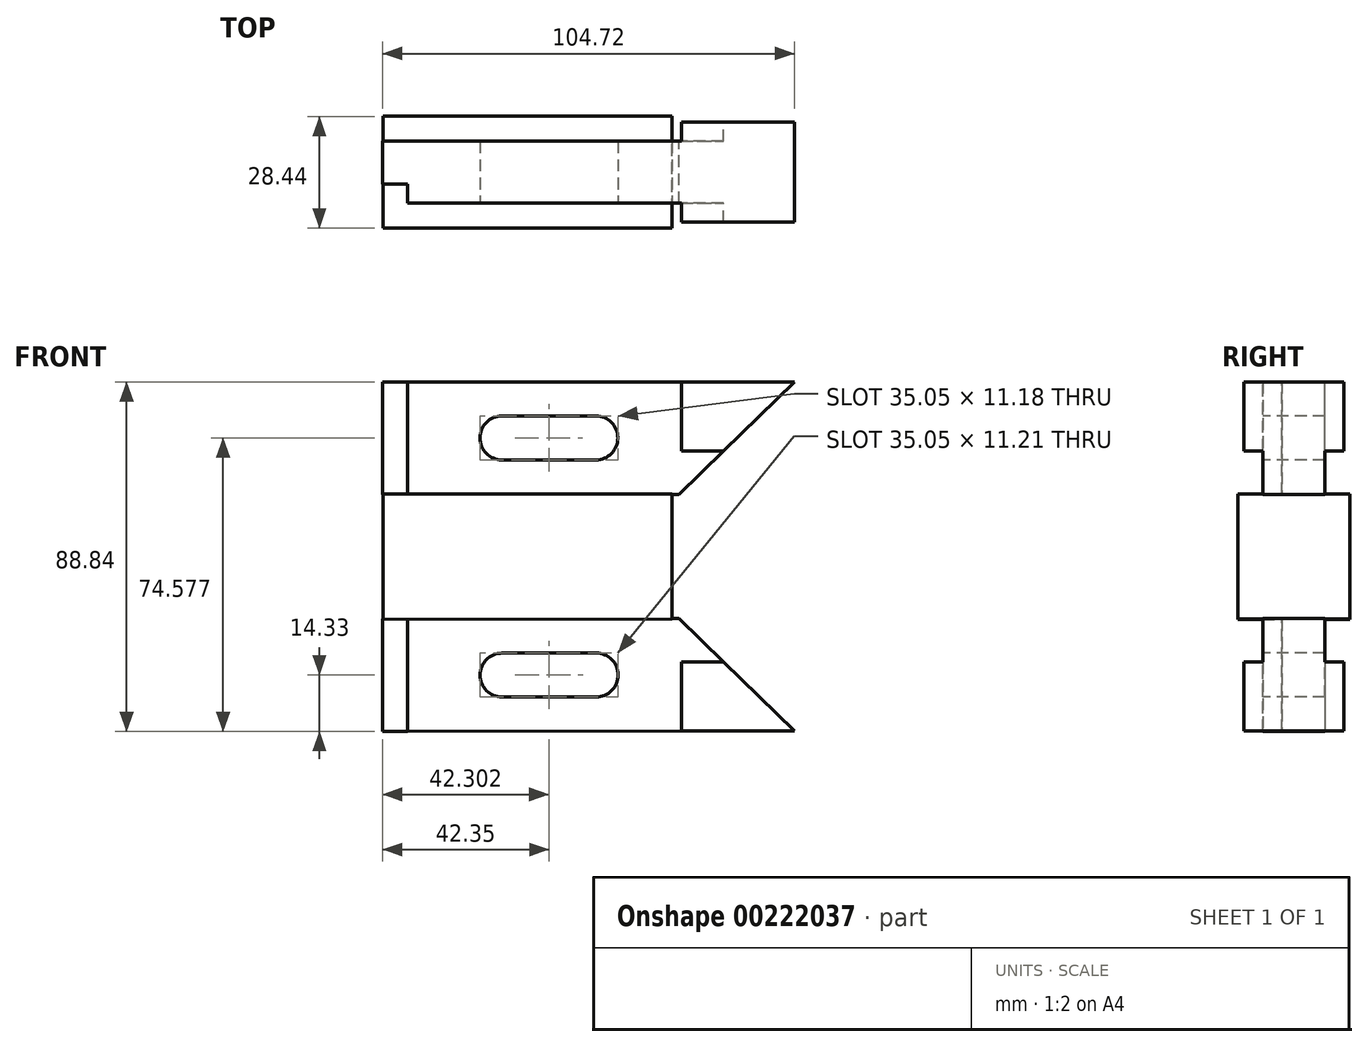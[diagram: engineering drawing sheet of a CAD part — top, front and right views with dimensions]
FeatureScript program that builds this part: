
annotation { "Feature Type Name" : "Feature", "Feature Type Description" : "" }
export const myFeature = defineFeature(function(context is Context, id is Id, definition is map)
    precondition{}
    {
        {
            var Q0;
            Q0=qCreatedBy(makeId("Front.planeOp"),FACE);
            var sketch = newSketch(context, id + "F0", { "sketchPlane" : qUnion([Q0])});
            skLineSegment(sketch, "E0", {"start": v(42.72, -44.4) * mm, "end": v(36.25, -44.4) * mm});
            skLineSegment(sketch, "E1", {"start": v(36.25, -44.4) * mm, "end": v(36.25, -15.82) * mm, "construction": true});
            skLineSegment(sketch, "E2", {"start": v(32.3, 15.93) * mm, "end": v(32.3, 0.06) * mm});
            skLineSegment(sketch, "E3", {"start": v(-41.1, 15.93) * mm, "end": v(-41.1, 0) * mm});
            skLineSegment(sketch, "E4", {"start": v(-41.1, 15.93) * mm, "end": v(32.3, 15.93) * mm});
            skLineSegment(sketch, "E5", {"start": v(32.3, 0.06) * mm, "end": v(-41.1, 0) * mm});
            skPoint(sketch, "E6.orphan", {"position": v(32.3, -15.82) * mm});
            skSolve(sketch);
        }
        {
            var Q0;
            Q0=makeQuery(id+"F0.imprint","IMPRINT",FACE,{"disambiguationData":[TD([[makeQuery(id+"F0.imprint","IMPRINT",EDGE,{"derivedFrom":sQuery(id+"F0.wireOp",EDGE,"E2")}),-1.0]])]});
            extrude(context, id + "F1", {"entities" : qUnion([Q0]), "endBound" : BoundingType.SYMMETRIC, "depth" : 28.45 * mm});
        }
        {
            var Q0;
            Q0=qCreatedBy(makeId("Front.planeOp"),FACE);
            var sketch = newSketch(context, id + "F2", { "sketchPlane" : qUnion([Q0])});
            skLineSegment(sketch, "E7.0", {"start": v(-41.1, 15.93) * mm, "end": v(32.3, 15.93) * mm});
            skLineSegment(sketch, "E8.bottom", {"start": v(-41.24, 15.85) * mm, "end": v(63.4, 15.85) * mm});
            skLineSegment(sketch, "E8.top", {"start": v(-41.24, 44.42) * mm, "end": v(63.4, 44.42) * mm});
            skLineSegment(sketch, "E8.left", {"start": v(-41.24, 15.85) * mm, "end": v(-41.24, 44.42) * mm});
            skLineSegment(sketch, "E8.right", {"start": v(63.4, 15.85) * mm, "end": v(63.4, 44.42) * mm});
            skSolve(sketch);
        }
        {
            var Q0;
            Q0=makeQuery(id+"F2.imprint","IMPRINT",FACE,{"disambiguationData":[TD([[makeQuery(id+"F2.imprint","IMPRINT",EDGE,{"derivedFrom":sQuery(id+"F2.wireOp",EDGE,"E8.bottom")}),1.0]])]});
            extrude(context, id + "F3", {"entities" : qUnion([Q0]), "operationType" : NewBodyOperationType.ADD, "endBound" : BoundingType.SYMMETRIC, "depth" : 15.75 * mm});
        }
        {
            var Q0;
            Q0=makeQuery(id+"F3.opExtrude","CAP_FACE",FACE,{"disambiguationData":[OSD([sQuery(id+"F2.wireOp",EDGE,"E8.bottom"),sQuery(id+"F2.wireOp",EDGE,"E8.top"),sQuery(id+"F2.wireOp",EDGE,"E8.left"),sQuery(id+"F2.wireOp",EDGE,"E8.right")])],"isStart":false});
            var sketch = newSketch(context, id + "F4", { "sketchPlane" : qUnion([Q0])});
            skLineSegment(sketch, "E9.bottom", {"start": v(-41.24, 44.42) * mm, "end": v(-34.9, 44.42) * mm});
            skLineSegment(sketch, "E9.top", {"start": v(-41.24, 15.85) * mm, "end": v(-34.9, 15.85) * mm});
            skLineSegment(sketch, "E9.left", {"start": v(-41.24, 44.42) * mm, "end": v(-41.24, 15.85) * mm});
            skLineSegment(sketch, "E9.right", {"start": v(-34.9, 44.42) * mm, "end": v(-34.9, 15.85) * mm});
            skSolve(sketch);
        }
        {
            var Q0;
            {var subQ2=sQuery(id+"F4.wireOp",EDGE,"E9.bottom");Q0=makeQuery(id+"F4.imprint","IMPRINT",FACE,{"disambiguationData":[TD([[makeQuery(id+"F4.imprint","IMPRINT",EDGE,{"derivedFrom":subQ2}),-1.0]])]});}
            extrude(context, id + "F5", {"entities" : qUnion([Q0]), "operationType" : NewBodyOperationType.REMOVE, "oppositeDirection" : true, "depth" : 4.83 * mm});
        }
        {
            var Q0;
            Q0=qCreatedBy(makeId("Front.planeOp"),FACE);
            var sketch = newSketch(context, id + "F6", { "sketchPlane" : qUnion([Q0])});
            skLineSegment(sketch, "E10.0", {"start": v(-34.9, 44.42) * mm, "end": v(63.4, 44.42) * mm});
            skLineSegment(sketch, "E11.bottom", {"start": v(34.7, 44.42) * mm, "end": v(63.4, 44.42) * mm});
            skLineSegment(sketch, "E11.top", {"start": v(34.7, 26.9) * mm, "end": v(63.4, 26.9) * mm});
            skLineSegment(sketch, "E11.left", {"start": v(34.7, 44.42) * mm, "end": v(34.7, 26.9) * mm});
            skLineSegment(sketch, "E11.right", {"start": v(63.4, 44.42) * mm, "end": v(63.4, 26.9) * mm});
            skSolve(sketch);
        }
        {
            var Q0;
            Q0 = qSketchRegion(id + "F6", true);
            extrude(context, id + "F7", {"entities" : qUnion([Q0]), "operationType" : NewBodyOperationType.ADD, "endBound" : BoundingType.SYMMETRIC, "depth" : 25.4 * mm});
        }
        {
            var Q0;
            Q0=qCreatedBy(makeId("Front.planeOp"),FACE);
            var sketch = newSketch(context, id + "F8", { "sketchPlane" : qUnion([Q0])});
            skPoint(sketch, "E12.0", {"position": v(63.4, 44.42) * mm});
            skPoint(sketch, "E13.0", {"position": v(63.4, 15.85) * mm});
            skPoint(sketch, "E14.0", {"position": v(32.3, 15.85) * mm});
            skLineSegment(sketch, "E15", {"start": v(34.05, 15.82) * mm, "end": v(63.4, 44.42) * mm});
            skLineSegment(sketch, "E16", {"start": v(34.05, 15.82) * mm, "end": v(63.4, 15.85) * mm});
            skLineSegment(sketch, "E17", {"start": v(63.4, 44.42) * mm, "end": v(63.4, 15.85) * mm});
            skSolve(sketch);
        }
        {
            var Q0;
            Q0 = qSketchRegion(id + "F8", true);
            extrude(context, id + "F9", {"entities" : qUnion([Q0]), "operationType" : NewBodyOperationType.REMOVE, "endBound" : BoundingType.SYMMETRIC, "oppositeDirection" : true, "depth" : 25.4 * mm});
        }
        {
            var Q0;
            Q0=makeQuery(id+"F3.opExtrude","CAP_FACE",FACE,{"disambiguationData":[OSD([sQuery(id+"F2.wireOp",EDGE,"E8.bottom"),sQuery(id+"F2.wireOp",EDGE,"E8.top"),sQuery(id+"F2.wireOp",EDGE,"E8.left"),sQuery(id+"F2.wireOp",EDGE,"E8.right")])],"isStart":false});
            var sketch = newSketch(context, id + "F10", { "sketchPlane" : qUnion([Q0])});
            skLineSegment(sketch, "E18.0.0", {"start": v(-34.9, 15.93) * mm, "end": v(-34.9, 44.42) * mm});
            skLineSegment(sketch, "E18.0.1", {"start": v(-34.9, 44.42) * mm, "end": v(-41.24, 44.42) * mm});
            skLineSegment(sketch, "E18.0.2", {"start": v(-41.24, 44.42) * mm, "end": v(-41.24, 15.85) * mm});
            skLineSegment(sketch, "E18.0.3", {"start": v(-41.24, 15.85) * mm, "end": v(-41.1, 15.85) * mm});
            skLineSegment(sketch, "E18.0.4", {"start": v(-41.1, 15.85) * mm, "end": v(-41.1, 15.93) * mm});
            skLineSegment(sketch, "E18.0.5", {"start": v(-41.1, 15.93) * mm, "end": v(-34.9, 15.93) * mm});
            skLineSegment(sketch, "E19.bottom", {"start": v(-10.88, 24.57) * mm, "end": v(13, 24.57) * mm});
            skLineSegment(sketch, "E19.top", {"start": v(-10.88, 35.74) * mm, "end": v(13, 35.74) * mm});
            skCircle(sketch, "E20", {"center": v(-10.88, 30.16) * mm, "radius": 5.59 * mm});
            skCircle(sketch, "E21", {"center": v(13, 30.16) * mm, "radius": 5.59 * mm});
            skSolve(sketch);
        }
        {
            var Q0;
            {var subQ0=sQuery(id+"F10.wireOp",EDGE,"E21");var subQ1=makeQuery(id+"F10.imprint","INTERSECT",VERTEX,{"derivedFrom":[sQuery(id+"F10.wireOp",EDGE,"E19.bottom"),subQ0]});Q0=makeQuery(id+"F10.imprint","IMPRINT",FACE,{"disambiguationData":[TD([[makeQuery(id+"F10.imprint","IMPRINT",EDGE,{"disambiguationData":[TD([[subQ1,1.0]])],"derivedFrom":subQ0}),1.0]])]});}
            var Q1;
            {var subQ0=sQuery(id+"F10.wireOp",EDGE,"E20");var subQ1=makeQuery(id+"F10.imprint","INTERSECT",VERTEX,{"derivedFrom":[sQuery(id+"F10.wireOp",EDGE,"E19.bottom"),subQ0]});Q1=makeQuery(id+"F10.imprint","IMPRINT",FACE,{"disambiguationData":[TD([[makeQuery(id+"F10.imprint","IMPRINT",EDGE,{"disambiguationData":[TD([[subQ1,1.0]])],"derivedFrom":subQ0}),1.0]])]});}
            var Q2;
            {var subQ0=sQuery(id+"F10.wireOp",EDGE,"E19.bottom");Q2=makeQuery(id+"F10.imprint","IMPRINT",FACE,{"disambiguationData":[TD([[makeQuery(id+"F10.imprint","IMPRINT",EDGE,{"derivedFrom":subQ0}),1.0]])]});}
            extrude(context, id + "F11", {"entities" : qUnion([Q0, Q1, Q2]), "operationType" : NewBodyOperationType.REMOVE, "oppositeDirection" : true, "depth" : 25.4 * mm});
        }
        {
            var Q0;
            Q0=makeQuery(id+"F1.opExtrude","SWEPT_BODY",BODY,{"disambiguationData":[OSD([sQuery(id+"F0.wireOp",EDGE,"E2"),sQuery(id+"F0.wireOp",EDGE,"E3"),sQuery(id+"F0.wireOp",EDGE,"E4"),sQuery(id+"F0.wireOp",EDGE,"E5")])]});
            var Q1;
            Q1=makeQuery(id+"F1.opExtrude","SWEPT_FACE",FACE,{"disambiguationData":[OSD([sQuery(id+"F0.wireOp",EDGE,"E5")])]});
            mirror(context, id + "F12", {"operationType" : NewBodyOperationType.ADD, "entities" : qUnion([Q0]), "mirrorPlane" : qUnion([Q1])});
        }
    });
